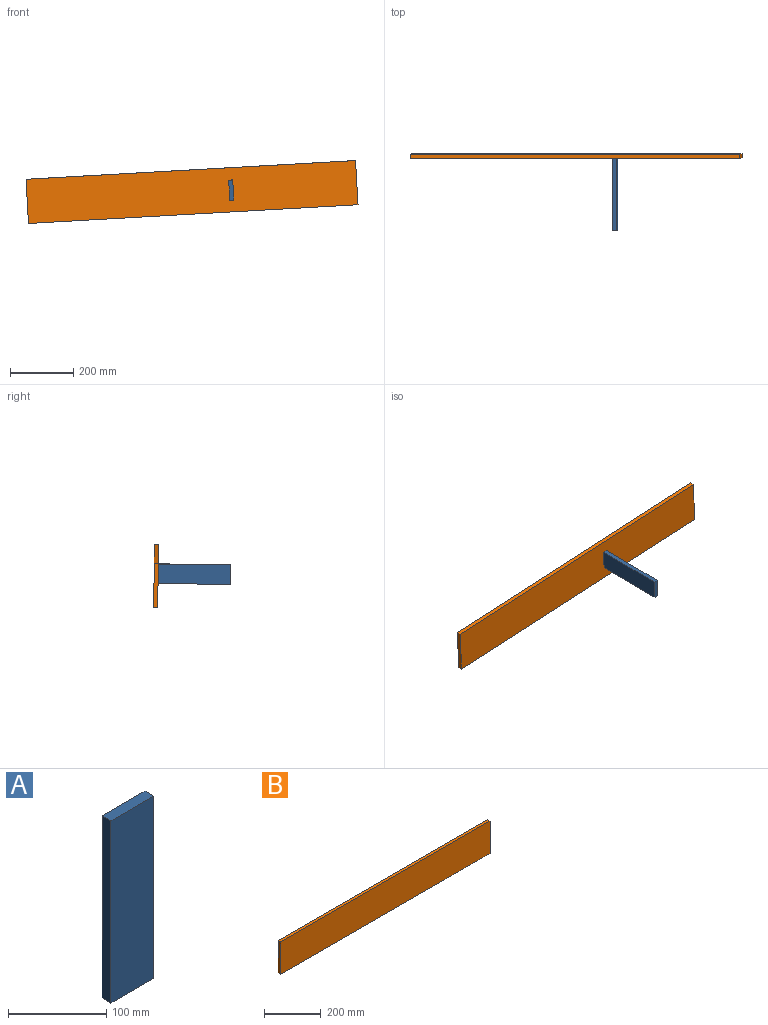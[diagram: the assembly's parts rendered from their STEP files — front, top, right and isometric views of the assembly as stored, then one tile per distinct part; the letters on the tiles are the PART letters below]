
ASSEMBLY  parts=2 mates=1
PART A: 6 faces, bbox 61.8x12.7x227.3 mm
  f0: plane 61.78x12.7mm, normal (0,0,-1), area 784.6mm2, adj f1,f3,f4,f5
  f1: plane 227.27x12.7mm, normal (1,0,0), area 2886.3mm2, adj f0,f2,f4,f5
  f2: plane 61.78x12.7mm, normal (0,0,1), area 784.6mm2, adj f1,f3,f4,f5
  f3: plane 227.27x12.7mm, normal (-1,0,0), area 2886.3mm2, adj f0,f2,f4,f5
  f4: plane 227.27x61.78mm, normal (0,-1,0), area 14040.9mm2, adj f0,f1,f2,f3
  f5: plane 227.27x61.78mm, normal (0,1,0), area 14040.9mm2, adj f0,f1,f2,f3
PART B: 6 faces, bbox 1041.4x12.7x139.7 mm
  f0: plane 139.7x12.7mm, normal (-1,0,0), area 1774.2mm2, adj f1,f3,f4,f5
  f1: plane 1041.4x12.7mm, normal (0,0,-1), area 13225.8mm2, adj f0,f2,f4,f5
  f2: plane 139.7x12.7mm, normal (1,0,0), area 1774.2mm2, adj f1,f3,f4,f5
  f3: plane 1041.4x12.7mm, normal (0,0,1), area 13225.8mm2, adj f0,f2,f4,f5
  f4: plane 1041.4x139.7mm, normal (0,-1,0), area 145483.6mm2, adj f0,f1,f2,f3
  f5: plane 1041.4x139.7mm, normal (0,1,0), area 145483.6mm2, adj f0,f1,f2,f3
PLACE A rot(axis=(0.6,0.57,-0.56),118.4deg) t=(22.2,132.54,-207.06)mm
PLACE B rot(axis=(0.15,-0.99,0),3.3deg) t=(-108.01,258.93,-213.38)mm
MATE planar B.f4 <-> A.f0  axis (0,-1,-0.01) through (-108.01,246.23,-213.49)mm
